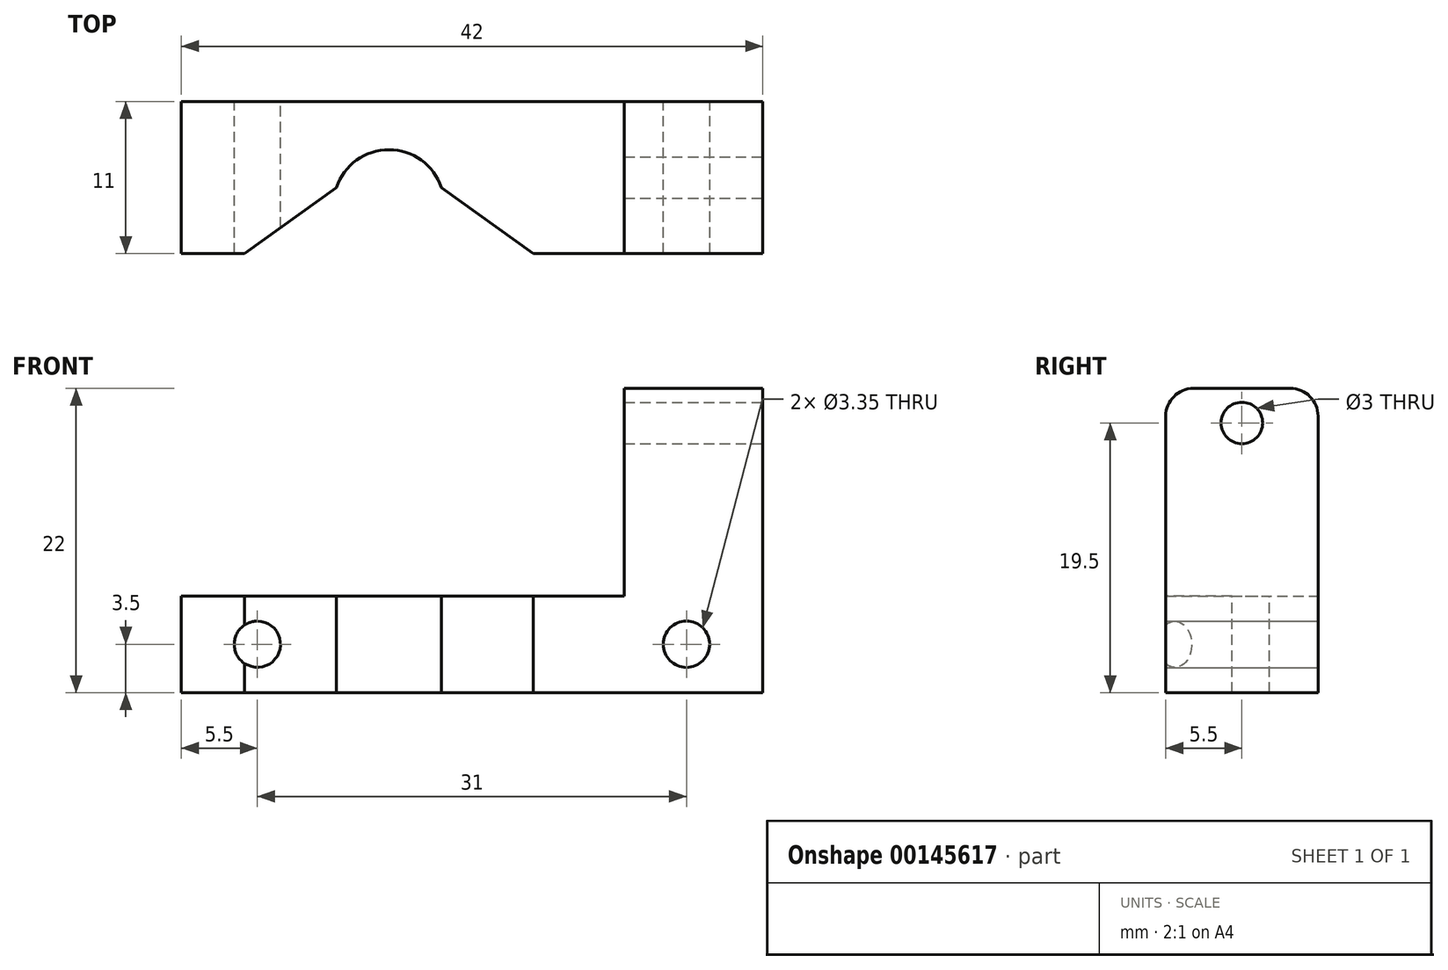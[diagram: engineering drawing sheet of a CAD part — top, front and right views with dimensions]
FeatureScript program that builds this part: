
annotation { "Feature Type Name" : "Feature", "Feature Type Description" : "" }
export const myFeature = defineFeature(function(context is Context, id is Id, definition is map)
    precondition{}
    {
        {
            assignVariable(context, id + "F0", {"name" : "rods", "anyValue" : 8});
        }
        {
            var Q0;
            Q0=qCreatedBy(makeId("Top.planeOp"),FACE);
            var sketch = newSketch(context, id + "F1", { "sketchPlane" : qUnion([Q0])});
            skLineSegment(sketch, "E0.bottom", {"start": v(0, 0) * mm, "end": v(42, 0) * mm});
            skLineSegment(sketch, "E0.top", {"start": v(0, 11) * mm, "end": v(42, 11) * mm});
            skLineSegment(sketch, "E0.left", {"start": v(0, 0) * mm, "end": v(0, 11) * mm});
            skLineSegment(sketch, "E0.right", {"start": v(42, 0) * mm, "end": v(42, 11) * mm});
            skSolve(sketch);
        }
        {
            var Q0;
            Q0=qSketchRegion(id+"F1",true);
            extrude(context, id + "F2", {"entities" : qUnion([Q0]), "depth" : 7 * mm});
        }
        {
            var Q0;
            Q0=makeQuery(id+"F2.opExtrude","CAP_FACE",FACE,{"disambiguationData":[OSD([sQuery(id+"F1.wireOp",EDGE,"E0.bottom"),sQuery(id+"F1.wireOp",EDGE,"E0.top"),sQuery(id+"F1.wireOp",EDGE,"E0.left"),sQuery(id+"F1.wireOp",EDGE,"E0.right")])],"isStart":false});
            var sketch = newSketch(context, id + "F3", { "sketchPlane" : qUnion([Q0])});
            skCircle(sketch, "E1", {"center": v(15, 3.5) * mm, "radius": 4 * mm});
            skSolve(sketch);
        }
        {
            var Q0;
            Q0=qSketchRegion(id+"F3",true);
            extrude(context, id + "F4", {"entities" : qUnion([Q0]), "operationType" : NewBodyOperationType.REMOVE, "oppositeDirection" : true, "depth" : 25 * mm});
        }
        {
            var Q0;
            Q0=makeQuery(id+"F4.boolean.opBoolean","INTERSECT",EDGE,{"disambiguationData":[OD(0.0)],"derivedFrom":[makeQuery(id+"F2.opExtrude","SWEPT_FACE",FACE,{"disambiguationData":[OSD([sQuery(id+"F1.wireOp",EDGE,"E0.bottom")])]}),makeQuery(id+"F4.opExtrude","SWEPT_FACE",FACE,{"disambiguationData":[OSD([sQuery(id+"F3.wireOp",EDGE,"E1")])]})]});
            var Q1;
            Q1=makeQuery(id+"F4.boolean.opBoolean","INTERSECT",EDGE,{"disambiguationData":[OD(1.0)],"derivedFrom":[makeQuery(id+"F2.opExtrude","SWEPT_FACE",FACE,{"disambiguationData":[OSD([sQuery(id+"F1.wireOp",EDGE,"E0.bottom")])]}),makeQuery(id+"F4.opExtrude","SWEPT_FACE",FACE,{"disambiguationData":[OSD([sQuery(id+"F3.wireOp",EDGE,"E1")])]})]});
            chamfer(context, id + "F5", {"entities" : qUnion([Q0, Q1]), "width" : (getVariable(context, 'rods') - 1) * mm, "tangentPropagation" : true});
        }
        {
            var Q0;
            Q0=makeQuery(id+"F2.opExtrude","SWEPT_FACE",FACE,{"disambiguationData":[OSD([sQuery(id+"F1.wireOp",EDGE,"E0.top")])]});
            var sketch = newSketch(context, id + "F6", { "sketchPlane" : qUnion([Q0])});
            skCircle(sketch, "E2", {"center": v(-5.5, 3.5) * mm, "radius": 1.68 * mm});
            skCircle(sketch, "E3", {"center": v(-36.5, 3.5) * mm, "radius": 1.68 * mm});
            skLineSegment(sketch, "E4", {"start": v(-5.5, 0) * mm, "end": v(-5.5, 7) * mm});
            skLineSegment(sketch, "E5", {"start": v(-5.5, 3.5) * mm, "end": v(0, 3.5) * mm});
            skLineSegment(sketch, "E6", {"start": v(-36.5, 3.5) * mm, "end": v(-42, 3.5) * mm});
            skSolve(sketch);
        }
        {
            var Q0;
            Q0=qSketchRegion(id+"F6",true);
            extrude(context, id + "F7", {"entities" : qUnion([Q0]), "operationType" : NewBodyOperationType.REMOVE, "oppositeDirection" : true, "depth" : 25 * mm});
        }
        {
            var Q0;
            Q0=makeQuery(id+"F2.opExtrude","CAP_FACE",FACE,{"disambiguationData":[OSD([sQuery(id+"F1.wireOp",EDGE,"E0.bottom"),sQuery(id+"F1.wireOp",EDGE,"E0.top"),sQuery(id+"F1.wireOp",EDGE,"E0.left"),sQuery(id+"F1.wireOp",EDGE,"E0.right")])],"isStart":false});
            var sketch = newSketch(context, id + "F8", { "sketchPlane" : qUnion([Q0])});
            skLineSegment(sketch, "E7.bottom", {"start": v(42, 0) * mm, "end": v(32, 0) * mm});
            skLineSegment(sketch, "E7.top", {"start": v(42, 11) * mm, "end": v(32, 11) * mm});
            skLineSegment(sketch, "E7.left", {"start": v(42, 0) * mm, "end": v(42, 11) * mm});
            skLineSegment(sketch, "E7.right", {"start": v(32, 0) * mm, "end": v(32, 11) * mm});
            skSolve(sketch);
        }
        {
            var Q0;
            Q0=qSketchRegion(id+"F8",true);
            extrude(context, id + "F9", {"entities" : qUnion([Q0]), "operationType" : NewBodyOperationType.ADD, "depth" : 15 * mm});
        }
        {
            var Q0;
            Q0=makeQuery(id+"FJdLS7F1L1csLPb_1.boolean.opBoolean","MERGE",FACE,{"derivedFrom":[makeQuery(id+"F9.boolean.opBoolean","MERGE",FACE,{"derivedFrom":[makeQuery(id+"F2.opExtrude","SWEPT_FACE",FACE,{"disambiguationData":[OSD([sQuery(id+"F1.wireOp",EDGE,"E0.right")])]}),makeQuery(id+"F9.opExtrude","SWEPT_FACE",FACE,{"disambiguationData":[OSD([sQuery(id+"F8.wireOp",EDGE,"E7.left")])]})]}),makeQuery(id+"FJdLS7F1L1csLPb_1.opExtrude","SWEPT_FACE",FACE,{"disambiguationData":[OSD([sQuery(id+"F4Ds6MLMi3WL0gL_1.wireOp",EDGE,"f6963c6d-1d98-4eef-b5cd-deae189cd3ae.left")])]})]});
            var sketch = newSketch(context, id + "F10", { "sketchPlane" : qUnion([Q0])});
            skCircle(sketch, "E8", {"center": v(5.5, 19.5) * mm, "radius": 1.5 * mm});
            skPoint(sketch, "E9", {"position": v(0, 19.5) * mm});
            skPoint(sketch, "E10", {"position": v(5.5, 0) * mm});
            skSolve(sketch);
        }
        {
            var Q0;
            Q0=qSketchRegion(id+"F10",true);
            extrude(context, id + "F11", {"entities" : qUnion([Q0]), "operationType" : NewBodyOperationType.REMOVE, "oppositeDirection" : true, "depth" : 25 * mm});
        }
        {
            var Q0;
            Q0=makeQuery(id+"F9.opExtrude","CAP_EDGE",EDGE,{"disambiguationData":[OSD([sQuery(id+"F8.wireOp",EDGE,"E7.bottom")])],"isStart":false});
            var Q1;
            Q1=makeQuery(id+"F9.opExtrude","CAP_EDGE",EDGE,{"disambiguationData":[OSD([sQuery(id+"F8.wireOp",EDGE,"E7.top")])],"isStart":false});
            fillet(context, id + "F12", {"entities" : qUnion([Q0, Q1]), "radius" : 2 * mm, "tangentPropagation" : true, "allowEdgeOverflow" : false});
        }
    });
